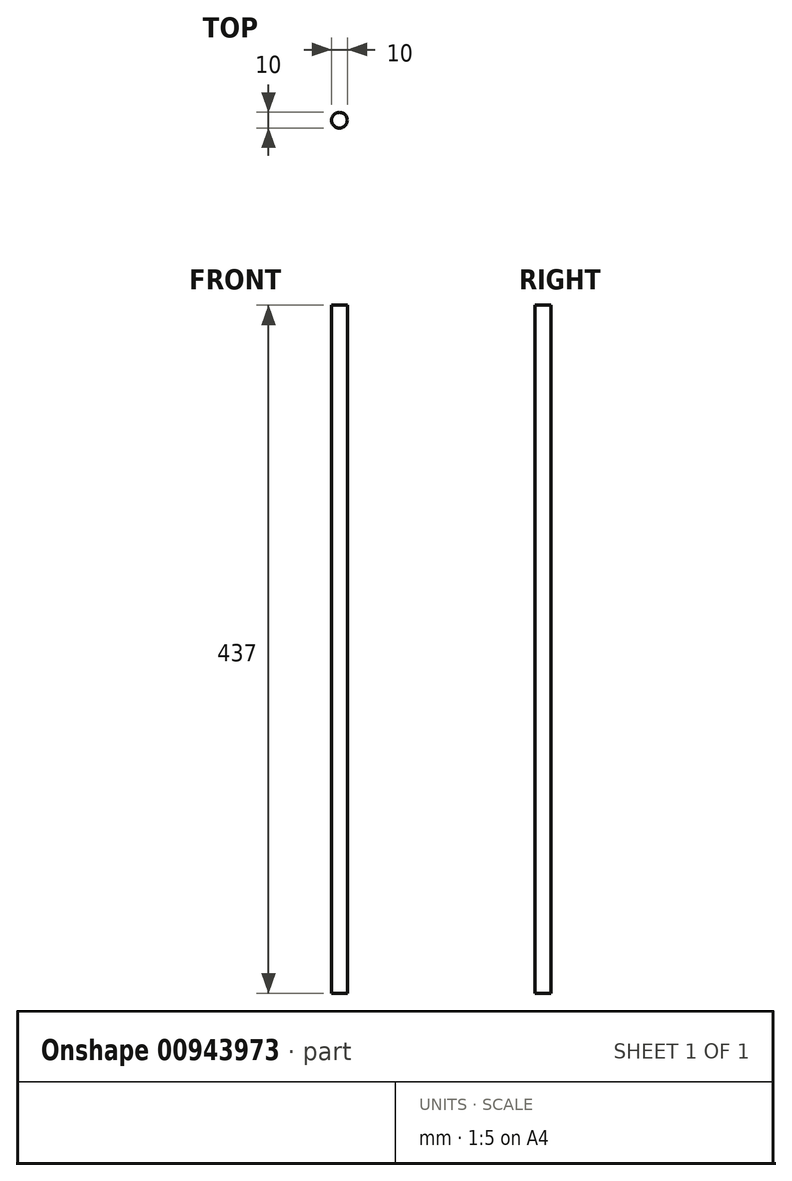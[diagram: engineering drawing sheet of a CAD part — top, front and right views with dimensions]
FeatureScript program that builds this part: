
annotation { "Feature Type Name" : "Feature", "Feature Type Description" : "" }
export const myFeature = defineFeature(function(context is Context, id is Id, definition is map)
    precondition{}
    {
        {
            var Q0;
            Q0=qCreatedBy(makeId("Top.planeOp"),FACE);
            var sketch = newSketch(context, id + "F0", { "sketchPlane" : qUnion([Q0])});
            skCircle(sketch, "E0", {"center": v(0, 0) * mm, "radius": 5 * mm});
            skSolve(sketch);
        }
        {
            var Q0;
            Q0=makeQuery(id+"F0.imprint","IMPRINT",FACE,{"disambiguationData":[TD([[makeQuery(id+"F0.imprint","IMPRINT",EDGE,{"derivedFrom":sQuery(id+"F0.wireOp",EDGE,"E0")}),1.0]])]});
            extrude(context, id + "F1", {"entities" : qUnion([Q0]), "flatOperationType" : FlatOperationType.REMOVE, "depth" : 437 * mm, "offsetDistance" : 25 * mm, "domain" : OperationDomain.MODEL});
        }
    });
